# Revit family: CFQ8-VER
name_source: partatom
category: Lighting Fixtures
revit_build: Autodesk Revit 2014 (Build: 20130308_1515(x64)
units: mm (PartAtom-declared; Revit-internal decimal feet)

## types (2) — shared parameters
Apparent Load = 27 VA
Assembly Code = D5020210
Color Filter = 16777215
Default Elevation = 22"
Description = 8'' Vertical Open, Wall Wash and Regressed Lensed Downlights
Dimming Lamp Color Temperature Shift = <None>
Emit Shape Visible in Rendering = No
Emit from Circle Diameter = 8"
Housing = Steel - Hubbell
Lamp = CFL
Load Classification = Lighting
Manufacturer = Prescolite
Model = CFQ8 Vertical
Photometric Notes = More IES files download on Photometric Web Link
Photometric Web File = CFT832EB.ies
Photometric Web Link = https://www.hubbell.com
Power Factor = 0.97
Product Documentation Link = https://hubbellcdn.com
Product Page URL = https://www.hubbell.com
Tilt Angle = -90.00°
URL = https://www.hubbell.com
Voltage = 120 V
Wattage Comments = 26W
Watts = 26 W

## per-type parameters (varying)
| type | Finish |
| CFQ826EB-Open & Wall Wash | Hubbell - Black |
| CFQ826EB-Regressed Lens | Steel - Hubbell |

## geometry (parser evidence)
native form markers: Blend x4, Sweep x4
no freeform markers — native parametric forms only
